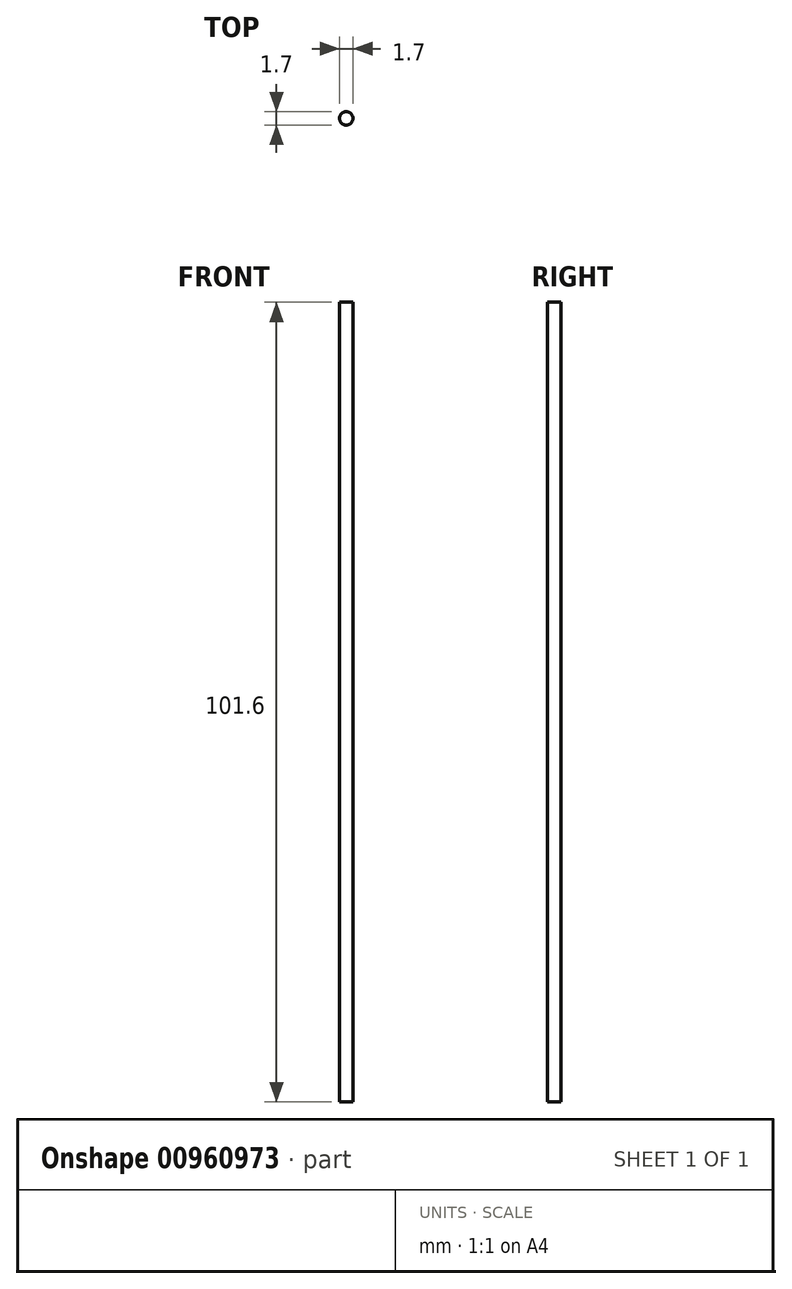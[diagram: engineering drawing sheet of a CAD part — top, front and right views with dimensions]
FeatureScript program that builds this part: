
annotation { "Feature Type Name" : "Feature", "Feature Type Description" : "" }
export const myFeature = defineFeature(function(context is Context, id is Id, definition is map)
    precondition{}
    {
        {
            var Q0;
            Q0=qCreatedBy(makeId("Top.planeOp"),FACE);
            var sketch = newSketch(context, id + "F0", { "sketchPlane" : qUnion([Q0])});
            skCircle(sketch, "E0", {"center": v(0, 0) * mm, "radius": 0.85 * mm});
            skCircle(sketch, "E1", {"center": v(0, 0) * mm, "radius": 1.27 * mm});
            skSolve(sketch);
        }
        {
            var Q0;
            Q0=makeQuery(id+"F0.imprint","IMPRINT",FACE,{"disambiguationData":[TD([[makeQuery(id+"F0.imprint","IMPRINT",EDGE,{"derivedFrom":sQuery(id+"F0.wireOp",EDGE,"E0")}),1.0]])]});
            extrude(context, id + "F1", {"entities" : qUnion([Q0]), "depth" : 101.6 * mm, "offsetDistance" : 25.4 * mm});
        }
    });
